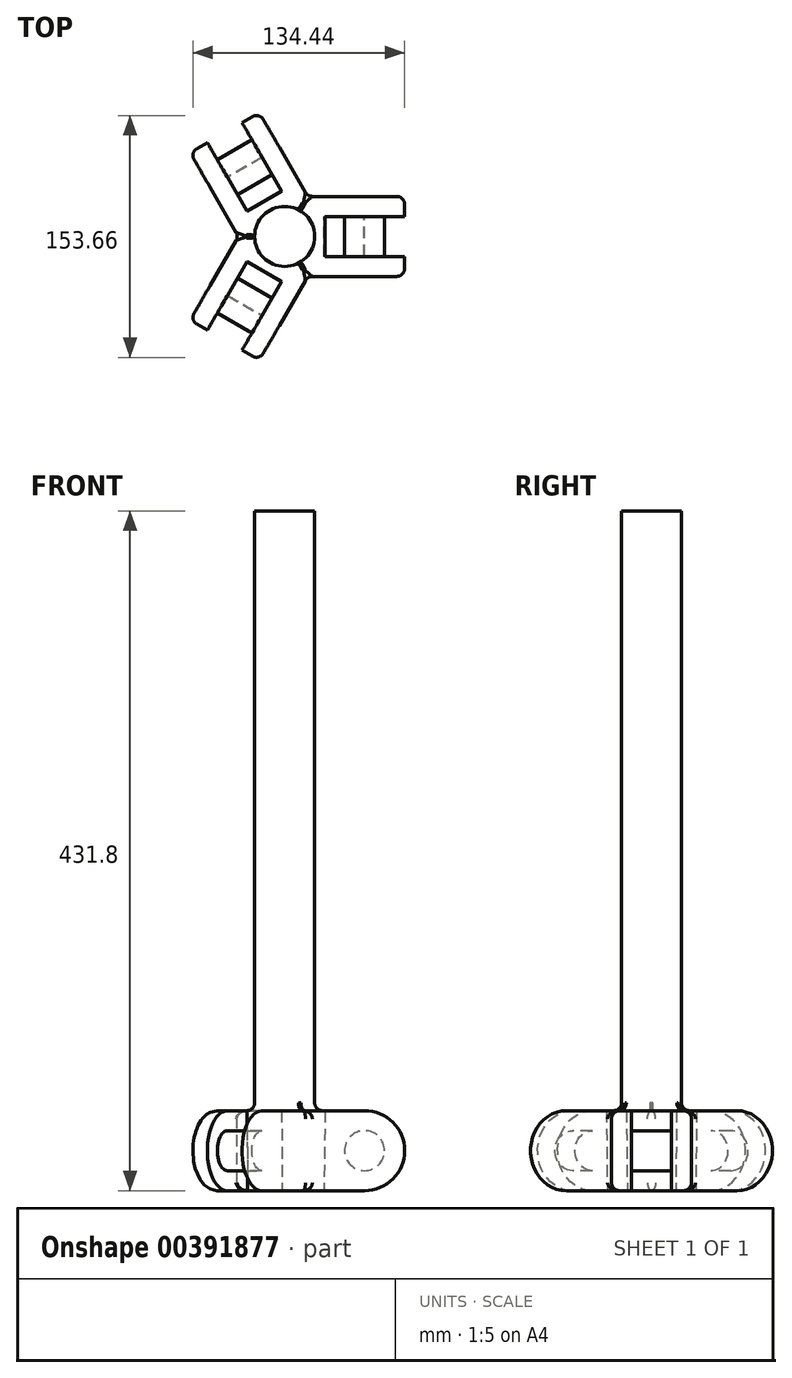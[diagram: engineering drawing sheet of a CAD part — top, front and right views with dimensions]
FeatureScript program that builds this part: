
annotation { "Feature Type Name" : "Feature", "Feature Type Description" : "" }
export const myFeature = defineFeature(function(context is Context, id is Id, definition is map)
    precondition{}
    {
        {
            var Q0;
            Q0=qCreatedBy(makeId("Front.planeOp"),FACE);
            var sketch = newSketch(context, id + "F0", { "sketchPlane" : qUnion([Q0])});
            skArc(sketch, "E0", {"start": v(50.8, -25.4) * mm, "mid": v(76.2, 0) * mm, "end": v(50.8, 25.4) * mm});
            skLineSegment(sketch, "E1.bottom", {"start": v(50.8, 25.4) * mm, "end": v(0, 25.4) * mm});
            skLineSegment(sketch, "E1.top", {"start": v(50.8, -25.4) * mm, "end": v(0, -25.4) * mm});
            skLineSegment(sketch, "E1.right", {"start": v(0, 25.4) * mm, "end": v(0, -25.4) * mm});
            skPoint(sketch, "E1.middle", {"position": v(25.4, 0) * mm});
            skSolve(sketch);
        }
        {
            var Q0;
            Q0 = qSketchRegion(id + "F0", true);
            extrude(context, id + "F1", {"entities" : qUnion([Q0]), "depth" : 25.4 * mm, "hasSecondDirection" : true, "secondDirectionOppositeDirection" : true, "secondDirectionDepth" : 25.4 * mm});
        }
        {
            var Q0;
            Q0=makeQuery(id+"F8.opPattern","COPY",EDGE,{"derivedFrom":makeQuery(id+"F1.opExtrude","CAP_EDGE",EDGE,{"disambiguationData":[OSD([sQuery(id+"F0.wireOp",EDGE,"E0")])],"isStart":true}),"instanceName":"2"});
            var Q1;
            Q1=makeQuery(id+"F8.opPattern","COPY",EDGE,{"derivedFrom":makeQuery(id+"F1.opExtrude","CAP_EDGE",EDGE,{"disambiguationData":[OSD([sQuery(id+"F0.wireOp",EDGE,"E0")])],"isStart":false}),"instanceName":"2"});
            var Q2;
            Q2=makeQuery(id+"F1.opExtrude","CAP_EDGE",EDGE,{"disambiguationData":[OSD([sQuery(id+"F0.wireOp",EDGE,"E0")])],"isStart":false});
            var Q3;
            Q3=makeQuery(id+"F1.opExtrude","CAP_EDGE",EDGE,{"disambiguationData":[OSD([sQuery(id+"F0.wireOp",EDGE,"E0")])],"isStart":true});
            fillet(context, id + "F2", {"entities" : qUnion([Q0, Q1, Q2, Q3]), "radius" : 5.08 * mm, "tangentPropagation" : true, "allowEdgeOverflow" : false});
        }
        {
            var Q0;
            Q0=qCreatedBy(makeId("Front.planeOp"),FACE);
            var sketch = newSketch(context, id + "F3", { "sketchPlane" : qUnion([Q0])});
            skCircle(sketch, "E2", {"center": v(50.8, 0) * mm, "radius": 12.7 * mm});
            skSolve(sketch);
        }
        {
            var Q0;
            Q0=qCreatedBy(makeId("Front.planeOp"),FACE);
            var sketch = newSketch(context, id + "F4", { "sketchPlane" : qUnion([Q0])});
            skArc(sketch, "E3", {"start": v(50.46, -25.4) * mm, "mid": v(76.2, -0.34) * mm, "end": v(51.14, 25.4) * mm});
            skLineSegment(sketch, "E4.bottom", {"start": v(51.14, 25.4) * mm, "end": v(25.74, 25.4) * mm});
            skLineSegment(sketch, "E4.top", {"start": v(50.46, -25.4) * mm, "end": v(25.06, -25.4) * mm});
            skLineSegment(sketch, "E4.right", {"start": v(25.74, 25.4) * mm, "end": v(25.06, -25.4) * mm});
            skPoint(sketch, "E4.middle", {"position": v(38.1, 0) * mm});
            skSolve(sketch);
        }
        {
            var Q0;
            Q0 = qSketchRegion(id + "F4", true);
            extrude(context, id + "F5", {"entities" : qUnion([Q0]), "operationType" : NewBodyOperationType.REMOVE, "depth" : 12.7 * mm, "hasSecondDirection" : true, "secondDirectionOppositeDirection" : true, "secondDirectionDepth" : 12.7 * mm});
        }
        {
            var Q0;
            Q0 = qSketchRegion(id + "F3", true);
            extrude(context, id + "F6", {"entities" : qUnion([Q0]), "operationType" : NewBodyOperationType.ADD, "depth" : 25.4 * mm, "hasSecondDirection" : true, "secondDirectionOppositeDirection" : true, "secondDirectionDepth" : 25.4 * mm});
        }
        {
            var Q0;
            Q0=qCreatedBy(makeId("Top.planeOp"),FACE);
            var sketch = newSketch(context, id + "F7", { "sketchPlane" : qUnion([Q0])});
            skCircle(sketch, "E5", {"center": v(0, 0) * mm, "radius": 19.08 * mm});
            skSolve(sketch);
        }
        {
            var Q0;
            Q0=makeQuery(id+"F1.opExtrude","SWEPT_BODY",BODY,{"disambiguationData":[OSD([sQuery(id+"F0.wireOp",EDGE,"E0"),sQuery(id+"F0.wireOp",EDGE,"E1.bottom"),sQuery(id+"F0.wireOp",EDGE,"E1.top"),sQuery(id+"F0.wireOp",EDGE,"E1.right")])]});
            var Q1;
            Q1=sQuery(id+"F7.wireOp",EDGE,"E5");
            circularPattern(context, id + "F8", {"operationType" : NewBodyOperationType.ADD, "entities" : qUnion([Q0]), "axis" : qUnion([Q1]), "angle" : 360 * degree, "instanceCount" : 3, "equalSpace" : true});
        }
        {
            var Q0;
            Q0=qCreatedBy(makeId("Top.planeOp"),FACE);
            var sketch = newSketch(context, id + "F9", { "sketchPlane" : qUnion([Q0])});
            skCircle(sketch, "E6", {"center": v(0, 0) * mm, "radius": 19.05 * mm});
            skSolve(sketch);
        }
        {
            var Q0;
            Q0 = qSketchRegion(id + "F9", true);
            extrude(context, id + "F10", {"entities" : qUnion([Q0]), "operationType" : NewBodyOperationType.ADD, "depth" : 182.88 * mm});
        }
        {
            var Q0;
            {var subQ0=sQuery(id+"F0.wireOp",EDGE,"E1.right");var subQ1=sQuery(id+"F0.wireOp",EDGE,"E1.top");var subQ2=sQuery(id+"F0.wireOp",EDGE,"E1.bottom");var subQ3=sQuery(id+"F0.wireOp",EDGE,"E0");Q0=makeQuery(id+"F8.boolean.opBoolean","INTERSECT",EDGE,{"derivedFrom":[makeQuery(id+"F1.opExtrude","CAP_FACE",FACE,{"disambiguationData":[OSD([subQ3,subQ2,subQ1,subQ0])],"isStart":false}),makeQuery(id+"F8.opPattern","COPY",FACE,{"derivedFrom":makeQuery(id+"F1.opExtrude","CAP_FACE",FACE,{"disambiguationData":[OSD([subQ3,subQ2,subQ1,subQ0])],"isStart":true}),"instanceName":"2"})]});}
            var Q1;
            {var subQ0=sQuery(id+"F0.wireOp",EDGE,"E1.right");var subQ1=sQuery(id+"F0.wireOp",EDGE,"E1.top");var subQ2=sQuery(id+"F0.wireOp",EDGE,"E1.bottom");var subQ3=sQuery(id+"F0.wireOp",EDGE,"E0");Q1=makeQuery(id+"F8.boolean.opBoolean","INTERSECT",EDGE,{"derivedFrom":[makeQuery(id+"F1.opExtrude","CAP_FACE",FACE,{"disambiguationData":[OSD([subQ3,subQ2,subQ1,subQ0])],"isStart":true}),makeQuery(id+"F8.opPattern","COPY",FACE,{"derivedFrom":makeQuery(id+"F1.opExtrude","CAP_FACE",FACE,{"disambiguationData":[OSD([subQ3,subQ2,subQ1,subQ0])],"isStart":false}),"instanceName":"1"})]});}
            var Q2;
            {var subQ0=sQuery(id+"F0.wireOp",EDGE,"E1.right");var subQ1=sQuery(id+"F0.wireOp",EDGE,"E1.top");var subQ2=sQuery(id+"F0.wireOp",EDGE,"E1.bottom");var subQ3=sQuery(id+"F0.wireOp",EDGE,"E0");Q2=makeQuery(id+"F8.boolean.opBoolean","INTERSECT",EDGE,{"derivedFrom":[makeQuery(id+"F8.opPattern","COPY",FACE,{"derivedFrom":makeQuery(id+"F1.opExtrude","CAP_FACE",FACE,{"disambiguationData":[OSD([subQ3,subQ2,subQ1,subQ0])],"isStart":true}),"instanceName":"1"}),makeQuery(id+"F8.opPattern","COPY",FACE,{"derivedFrom":makeQuery(id+"F1.opExtrude","CAP_FACE",FACE,{"disambiguationData":[OSD([subQ3,subQ2,subQ1,subQ0])],"isStart":false}),"instanceName":"2"})]});}
            fillet(context, id + "F11", {"entities" : qUnion([Q0, Q1, Q2]), "radius" : 5.08 * mm, "tangentPropagation" : true, "allowEdgeOverflow" : false});
        }
        {
            var Q0;
            {var subQ0=makeQuery(id+"F1.opExtrude","SWEPT_FACE",FACE,{"disambiguationData":[OSD([sQuery(id+"F0.wireOp",EDGE,"E1.bottom")])]});Q0=makeQuery(id+"F10.boolean.opBoolean","INTERSECT",EDGE,{"disambiguationData":[OD(2.0)],"derivedFrom":[makeQuery(id+"F8.boolean.opBoolean","MERGE",FACE,{"derivedFrom":[subQ0,makeQuery(id+"F8.opPattern","COPY",FACE,{"derivedFrom":subQ0,"instanceName":"1"}),makeQuery(id+"F8.opPattern","COPY",FACE,{"derivedFrom":subQ0,"instanceName":"2"})]}),makeQuery(id+"F10.opExtrude","SWEPT_FACE",FACE,{"disambiguationData":[OSD([sQuery(id+"F9.wireOp",EDGE,"E6")])]})]});}
            var Q1;
            {var subQ0=makeQuery(id+"F1.opExtrude","SWEPT_FACE",FACE,{"disambiguationData":[OSD([sQuery(id+"F0.wireOp",EDGE,"E1.bottom")])]});Q1=makeQuery(id+"F10.boolean.opBoolean","INTERSECT",EDGE,{"disambiguationData":[OD(1.0)],"derivedFrom":[makeQuery(id+"F8.boolean.opBoolean","MERGE",FACE,{"derivedFrom":[subQ0,makeQuery(id+"F8.opPattern","COPY",FACE,{"derivedFrom":subQ0,"instanceName":"1"}),makeQuery(id+"F8.opPattern","COPY",FACE,{"derivedFrom":subQ0,"instanceName":"2"})]}),makeQuery(id+"F10.opExtrude","SWEPT_FACE",FACE,{"disambiguationData":[OSD([sQuery(id+"F9.wireOp",EDGE,"E6")])]})]});}
            var Q2;
            {var subQ0=makeQuery(id+"F1.opExtrude","SWEPT_FACE",FACE,{"disambiguationData":[OSD([sQuery(id+"F0.wireOp",EDGE,"E1.bottom")])]});Q2=makeQuery(id+"F10.boolean.opBoolean","INTERSECT",EDGE,{"disambiguationData":[OD(0.0)],"derivedFrom":[makeQuery(id+"F8.boolean.opBoolean","MERGE",FACE,{"derivedFrom":[subQ0,makeQuery(id+"F8.opPattern","COPY",FACE,{"derivedFrom":subQ0,"instanceName":"1"}),makeQuery(id+"F8.opPattern","COPY",FACE,{"derivedFrom":subQ0,"instanceName":"2"})]}),makeQuery(id+"F10.opExtrude","SWEPT_FACE",FACE,{"disambiguationData":[OSD([sQuery(id+"F9.wireOp",EDGE,"E6")])]})]});}
            fillet(context, id + "F12", {"entities" : qUnion([Q0, Q1, Q2]), "radius" : 5.08 * mm, "tangentPropagation" : true, "allowEdgeOverflow" : false});
        }
        {
            var Q0;
            Q0=makeQuery(id+"F10.opExtrude","CAP_FACE",FACE,{"disambiguationData":[OSD([sQuery(id+"F9.wireOp",EDGE,"E6")])],"isStart":false});
            extrude(context, id + "F13", {"entities" : qUnion([Q0]), "operationType" : NewBodyOperationType.ADD, "depth" : 223.52 * mm});
        }
    });
